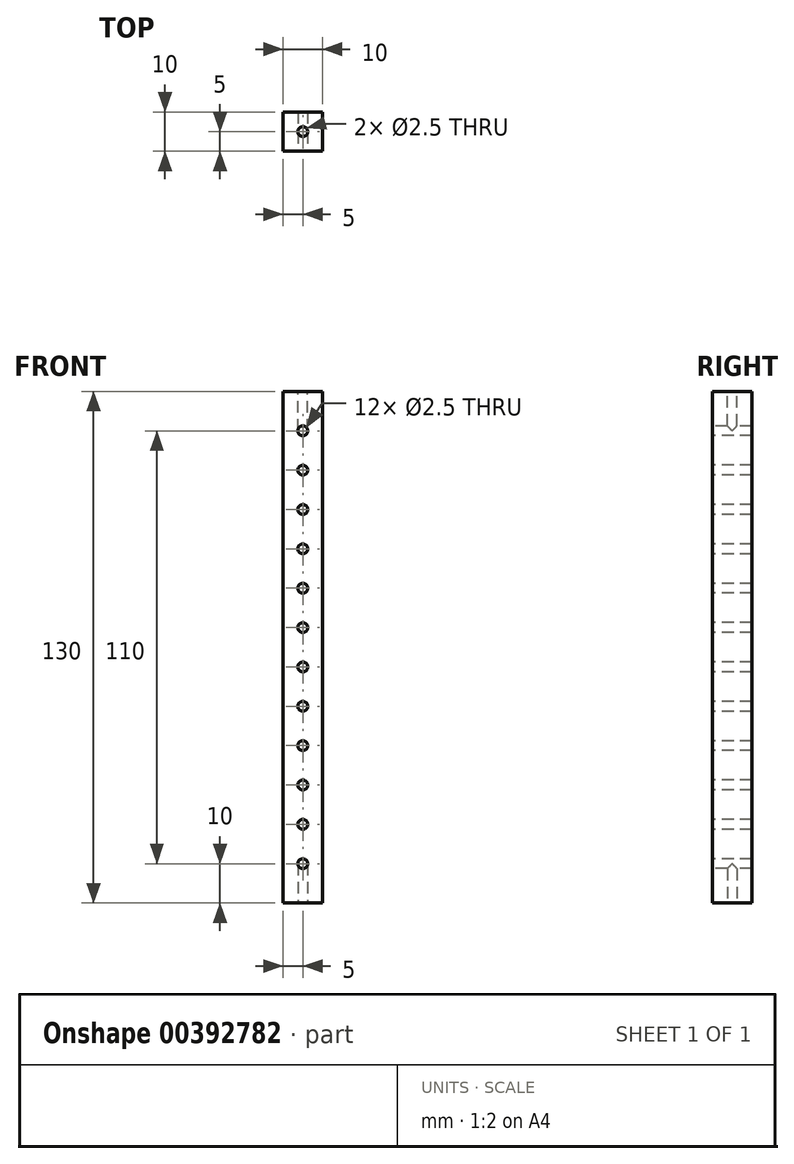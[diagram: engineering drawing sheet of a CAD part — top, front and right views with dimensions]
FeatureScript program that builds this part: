
annotation { "Feature Type Name" : "Feature", "Feature Type Description" : "" }
export const myFeature = defineFeature(function(context is Context, id is Id, definition is map)
    precondition{}
    {
        {
            var Q0;
            Q0=qCreatedBy(makeId("Top.planeOp"),FACE);
            var sketch = newSketch(context, id + "F0", { "sketchPlane" : qUnion([Q0])});
            skLineSegment(sketch, "E0.bottom", {"start": v(0, 0) * mm, "end": v(10, 0) * mm});
            skLineSegment(sketch, "E0.top", {"start": v(0, 10) * mm, "end": v(10, 10) * mm});
            skLineSegment(sketch, "E0.left", {"start": v(0, 0) * mm, "end": v(0, 10) * mm});
            skLineSegment(sketch, "E0.right", {"start": v(10, 0) * mm, "end": v(10, 10) * mm});
            skSolve(sketch);
        }
        {
            var Q0;
            Q0=makeQuery(id+"F0.imprint","IMPRINT",FACE,{"disambiguationData":[TD([[makeQuery(id+"F0.imprint","IMPRINT",EDGE,{"derivedFrom":sQuery(id+"F0.wireOp",EDGE,"E0.bottom")}),1.0]])]});
            extrude(context, id + "F1", {"entities" : qUnion([Q0]), "depth" : 130 * mm});
        }
        {
            var Q0;
            Q0=makeQuery(id+"F1.opExtrude","SWEPT_FACE",FACE,{"disambiguationData":[OSD([sQuery(id+"F0.wireOp",EDGE,"E0.bottom")])]});
            var sketch = newSketch(context, id + "F2", { "sketchPlane" : qUnion([Q0])});
            skLineSegment(sketch, "E1.bottom", {"start": v(0, 0) * mm, "end": v(5, 0) * mm});
            skLineSegment(sketch, "E1.top", {"start": v(0, 10) * mm, "end": v(5, 10) * mm});
            skLineSegment(sketch, "E1.left", {"start": v(0, 0) * mm, "end": v(0, 10) * mm});
            skLineSegment(sketch, "E1.right", {"start": v(5, 0) * mm, "end": v(5, 10) * mm});
            skLineSegment(sketch, "E2.bottom", {"start": v(5, 10) * mm, "end": v(10, 10) * mm});
            skLineSegment(sketch, "E2.top", {"start": v(5, 20) * mm, "end": v(10, 20) * mm});
            skLineSegment(sketch, "E2.left", {"start": v(5, 10) * mm, "end": v(5, 20) * mm});
            skLineSegment(sketch, "E2.right", {"start": v(10, 10) * mm, "end": v(10, 20) * mm});
            skLineSegment(sketch, "E3.bottom", {"start": v(5, 20) * mm, "end": v(0, 20) * mm});
            skLineSegment(sketch, "E3.top", {"start": v(5, 30) * mm, "end": v(0, 30) * mm});
            skLineSegment(sketch, "E3.left", {"start": v(5, 20) * mm, "end": v(5, 30) * mm});
            skLineSegment(sketch, "E3.right", {"start": v(0, 20) * mm, "end": v(0, 30) * mm});
            skSolve(sketch);
        }
        {
            var Q0;
            Q0=sQuery(id+"F2.wireOp",VERTEX,"E1.top.end");
            var Q1;
            Q1=sQuery(id+"F2.wireOp",VERTEX,"E3.bottom.start");
            var Q2;
            Q2=sQuery(id+"F2.wireOp",VERTEX,"E3.top.start");
            var Q3;
            Q3=makeQuery(id+"F1.opExtrude","SWEPT_BODY",BODY,{"disambiguationData":[OSD([sQuery(id+"F0.wireOp",EDGE,"E0.bottom"),sQuery(id+"F0.wireOp",EDGE,"E0.top"),sQuery(id+"F0.wireOp",EDGE,"E0.left"),sQuery(id+"F0.wireOp",EDGE,"E0.right")])]});
            hole(context, id + "F3", {"style" : HoleStyle.SIMPLE, "endStyle" : HoleEndStyle.BLIND, "holeDiameter" : 2.5 * mm, "holeDepth" : 10 * mm, "isTappedThrough" : true, "tappedDepth" : 12 * mm, "tapClearance" : 3, "locations" : qUnion([Q0, Q1, Q2]), "scope" : qUnion([Q3])});
        }
        {
            var Q0;
            Q0=makeQuery(id+"F1.opExtrude","SWEPT_FACE",FACE,{"disambiguationData":[OSD([sQuery(id+"F0.wireOp",EDGE,"E0.bottom")])]});
            var sketch = newSketch(context, id + "F4", { "sketchPlane" : qUnion([Q0])});
            skLineSegment(sketch, "E4.bottom", {"start": v(5, 30) * mm, "end": v(10, 30) * mm});
            skLineSegment(sketch, "E4.top", {"start": v(5, 40) * mm, "end": v(10, 40) * mm});
            skLineSegment(sketch, "E4.left", {"start": v(5, 30) * mm, "end": v(5, 40) * mm});
            skLineSegment(sketch, "E4.right", {"start": v(10, 30) * mm, "end": v(10, 40) * mm});
            skLineSegment(sketch, "E5.bottom", {"start": v(5, 40) * mm, "end": v(0, 40) * mm});
            skLineSegment(sketch, "E5.top", {"start": v(5, 50) * mm, "end": v(0, 50) * mm});
            skLineSegment(sketch, "E5.left", {"start": v(5, 40) * mm, "end": v(5, 50) * mm});
            skLineSegment(sketch, "E5.right", {"start": v(0, 40) * mm, "end": v(0, 50) * mm});
            skLineSegment(sketch, "E6.bottom", {"start": v(5, 50) * mm, "end": v(10, 50) * mm});
            skLineSegment(sketch, "E6.top", {"start": v(5, 60) * mm, "end": v(10, 60) * mm});
            skLineSegment(sketch, "E6.left", {"start": v(5, 50) * mm, "end": v(5, 60) * mm});
            skLineSegment(sketch, "E6.right", {"start": v(10, 50) * mm, "end": v(10, 60) * mm});
            skSolve(sketch);
        }
        {
            var Q0;
            Q0=sQuery(id+"F4.wireOp",VERTEX,"E4.top.start");
            var Q1;
            Q1=sQuery(id+"F4.wireOp",VERTEX,"E6.bottom.start");
            var Q2;
            Q2=sQuery(id+"F4.wireOp",VERTEX,"E6.top.start");
            var Q3;
            Q3=makeQuery(id+"F1.opExtrude","SWEPT_BODY",BODY,{"disambiguationData":[OSD([sQuery(id+"F0.wireOp",EDGE,"E0.bottom"),sQuery(id+"F0.wireOp",EDGE,"E0.top"),sQuery(id+"F0.wireOp",EDGE,"E0.left"),sQuery(id+"F0.wireOp",EDGE,"E0.right")])]});
            hole(context, id + "F5", {"style" : HoleStyle.SIMPLE, "endStyle" : HoleEndStyle.BLIND, "holeDiameter" : 2.5 * mm, "holeDepth" : 10 * mm, "isTappedThrough" : true, "tappedDepth" : 12 * mm, "tapClearance" : 3, "locations" : qUnion([Q0, Q1, Q2]), "scope" : qUnion([Q3])});
        }
        {
            var Q0;
            Q0=makeQuery(id+"F1.opExtrude","SWEPT_FACE",FACE,{"disambiguationData":[OSD([sQuery(id+"F0.wireOp",EDGE,"E0.bottom")])]});
            var sketch = newSketch(context, id + "F6", { "sketchPlane" : qUnion([Q0])});
            skLineSegment(sketch, "E7.bottom", {"start": v(5, 60) * mm, "end": v(10, 60) * mm});
            skLineSegment(sketch, "E7.top", {"start": v(5, 70) * mm, "end": v(10, 70) * mm});
            skLineSegment(sketch, "E7.left", {"start": v(5, 60) * mm, "end": v(5, 70) * mm});
            skLineSegment(sketch, "E7.right", {"start": v(10, 60) * mm, "end": v(10, 70) * mm});
            skLineSegment(sketch, "E8.bottom", {"start": v(5, 70) * mm, "end": v(0, 70) * mm});
            skLineSegment(sketch, "E8.top", {"start": v(5, 80) * mm, "end": v(0, 80) * mm});
            skLineSegment(sketch, "E8.left", {"start": v(5, 70) * mm, "end": v(5, 80) * mm});
            skLineSegment(sketch, "E8.right", {"start": v(0, 70) * mm, "end": v(0, 80) * mm});
            skLineSegment(sketch, "E9.bottom", {"start": v(5, 80) * mm, "end": v(10, 80) * mm});
            skLineSegment(sketch, "E9.top", {"start": v(5, 90) * mm, "end": v(10, 90) * mm});
            skLineSegment(sketch, "E9.left", {"start": v(5, 80) * mm, "end": v(5, 90) * mm});
            skLineSegment(sketch, "E9.right", {"start": v(10, 80) * mm, "end": v(10, 90) * mm});
            skLineSegment(sketch, "E10.bottom", {"start": v(5, 90) * mm, "end": v(0, 90) * mm});
            skLineSegment(sketch, "E10.top", {"start": v(5, 100) * mm, "end": v(0, 100) * mm});
            skLineSegment(sketch, "E10.left", {"start": v(5, 90) * mm, "end": v(5, 100) * mm});
            skLineSegment(sketch, "E10.right", {"start": v(0, 90) * mm, "end": v(0, 100) * mm});
            skLineSegment(sketch, "E11.bottom", {"start": v(5, 100) * mm, "end": v(10, 100) * mm});
            skLineSegment(sketch, "E11.top", {"start": v(5, 110) * mm, "end": v(10, 110) * mm});
            skLineSegment(sketch, "E11.left", {"start": v(5, 100) * mm, "end": v(5, 110) * mm});
            skLineSegment(sketch, "E11.right", {"start": v(10, 100) * mm, "end": v(10, 110) * mm});
            skSolve(sketch);
        }
        {
            var Q0;
            Q0=sQuery(id+"F6.wireOp",VERTEX,"E8.top.start");
            var Q1;
            Q1=sQuery(id+"F6.wireOp",VERTEX,"E10.bottom.start");
            var Q2;
            Q2=sQuery(id+"F6.wireOp",VERTEX,"E10.top.start");
            var Q3;
            Q3=sQuery(id+"F6.wireOp",VERTEX,"E11.left.end");
            var Q4;
            Q4=makeQuery(id+"F1.opExtrude","SWEPT_BODY",BODY,{"disambiguationData":[OSD([sQuery(id+"F0.wireOp",EDGE,"E0.bottom"),sQuery(id+"F0.wireOp",EDGE,"E0.top"),sQuery(id+"F0.wireOp",EDGE,"E0.left"),sQuery(id+"F0.wireOp",EDGE,"E0.right")])]});
            hole(context, id + "F7", {"style" : HoleStyle.SIMPLE, "endStyle" : HoleEndStyle.BLIND, "holeDiameter" : 2.5 * mm, "holeDepth" : 10 * mm, "isTappedThrough" : true, "tappedDepth" : 12 * mm, "tapClearance" : 3, "locations" : qUnion([Q0, Q1, Q2, Q3]), "scope" : qUnion([Q4])});
        }
        {
            var Q0;
            Q0=makeQuery(id+"F1.opExtrude","SWEPT_FACE",FACE,{"disambiguationData":[OSD([sQuery(id+"F0.wireOp",EDGE,"E0.bottom")])]});
            var sketch = newSketch(context, id + "F8", { "sketchPlane" : qUnion([Q0])});
            skLineSegment(sketch, "E12.bottom", {"start": v(5, 80) * mm, "end": v(10, 80) * mm});
            skLineSegment(sketch, "E12.top", {"start": v(5, 70) * mm, "end": v(10, 70) * mm});
            skLineSegment(sketch, "E12.left", {"start": v(5, 80) * mm, "end": v(5, 70) * mm});
            skLineSegment(sketch, "E12.right", {"start": v(10, 80) * mm, "end": v(10, 70) * mm});
            skSolve(sketch);
        }
        {
            var Q0;
            Q0=sQuery(id+"F8.wireOp",VERTEX,"E12.left.end");
            var Q1;
            Q1=makeQuery(id+"F1.opExtrude","SWEPT_BODY",BODY,{"disambiguationData":[OSD([sQuery(id+"F0.wireOp",EDGE,"E0.bottom"),sQuery(id+"F0.wireOp",EDGE,"E0.top"),sQuery(id+"F0.wireOp",EDGE,"E0.left"),sQuery(id+"F0.wireOp",EDGE,"E0.right")])]});
            hole(context, id + "F9", {"style" : HoleStyle.SIMPLE, "endStyle" : HoleEndStyle.BLIND, "holeDiameter" : 2.5 * mm, "holeDepth" : 10 * mm, "isTappedThrough" : true, "tappedDepth" : 12 * mm, "tapClearance" : 3, "locations" : qUnion([Q0]), "scope" : qUnion([Q1])});
        }
        {
            var Q0;
            Q0=makeQuery(id+"F1.opExtrude","SWEPT_FACE",FACE,{"disambiguationData":[OSD([sQuery(id+"F0.wireOp",EDGE,"E0.bottom")])]});
            var sketch = newSketch(context, id + "F10", { "sketchPlane" : qUnion([Q0])});
            skLineSegment(sketch, "E13.bottom", {"start": v(5, 110) * mm, "end": v(0, 110) * mm});
            skLineSegment(sketch, "E13.top", {"start": v(5, 120) * mm, "end": v(0, 120) * mm});
            skLineSegment(sketch, "E13.left", {"start": v(5, 110) * mm, "end": v(5, 120) * mm});
            skLineSegment(sketch, "E13.right", {"start": v(0, 110) * mm, "end": v(0, 120) * mm});
            skSolve(sketch);
        }
        {
            var Q0;
            Q0=sQuery(id+"F10.wireOp",VERTEX,"E13.top.start");
            var Q1;
            Q1=makeQuery(id+"F1.opExtrude","SWEPT_BODY",BODY,{"disambiguationData":[OSD([sQuery(id+"F0.wireOp",EDGE,"E0.bottom"),sQuery(id+"F0.wireOp",EDGE,"E0.top"),sQuery(id+"F0.wireOp",EDGE,"E0.left"),sQuery(id+"F0.wireOp",EDGE,"E0.right")])]});
            hole(context, id + "F11", {"style" : HoleStyle.SIMPLE, "endStyle" : HoleEndStyle.BLIND, "holeDiameter" : 2.5 * mm, "holeDepth" : 10 * mm, "isTappedThrough" : true, "tappedDepth" : 12 * mm, "tapClearance" : 3, "locations" : qUnion([Q0]), "scope" : qUnion([Q1])});
        }
        {
            var Q0;
            Q0=makeQuery(id+"F1.opExtrude","CAP_FACE",FACE,{"disambiguationData":[OSD([sQuery(id+"F0.wireOp",EDGE,"E0.bottom"),sQuery(id+"F0.wireOp",EDGE,"E0.top"),sQuery(id+"F0.wireOp",EDGE,"E0.left"),sQuery(id+"F0.wireOp",EDGE,"E0.right")])],"isStart":false});
            var sketch = newSketch(context, id + "F12", { "sketchPlane" : qUnion([Q0])});
            skLineSegment(sketch, "E14.bottom", {"start": v(0, 0) * mm, "end": v(5, 0) * mm});
            skLineSegment(sketch, "E14.top", {"start": v(0, 5) * mm, "end": v(5, 5) * mm});
            skLineSegment(sketch, "E14.left", {"start": v(0, 0) * mm, "end": v(0, 5) * mm});
            skLineSegment(sketch, "E14.right", {"start": v(5, 0) * mm, "end": v(5, 5) * mm});
            skSolve(sketch);
        }
        {
            var Q0;
            Q0=sQuery(id+"F12.wireOp",VERTEX,"E14.top.end");
            var Q1;
            Q1=makeQuery(id+"F1.opExtrude","SWEPT_BODY",BODY,{"disambiguationData":[OSD([sQuery(id+"F0.wireOp",EDGE,"E0.bottom"),sQuery(id+"F0.wireOp",EDGE,"E0.top"),sQuery(id+"F0.wireOp",EDGE,"E0.left"),sQuery(id+"F0.wireOp",EDGE,"E0.right")])]});
            hole(context, id + "F13", {"style" : HoleStyle.SIMPLE, "endStyle" : HoleEndStyle.BLIND, "holeDiameter" : 2.5 * mm, "holeDepth" : 10 * mm, "isTappedThrough" : true, "tappedDepth" : 12 * mm, "tapClearance" : 3, "locations" : qUnion([Q0]), "scope" : qUnion([Q1])});
        }
        {
            var Q0;
            Q0=makeQuery(id+"F1.opExtrude","CAP_FACE",FACE,{"disambiguationData":[OSD([sQuery(id+"F0.wireOp",EDGE,"E0.bottom"),sQuery(id+"F0.wireOp",EDGE,"E0.top"),sQuery(id+"F0.wireOp",EDGE,"E0.left"),sQuery(id+"F0.wireOp",EDGE,"E0.right")])],"isStart":true});
            var sketch = newSketch(context, id + "F14", { "sketchPlane" : qUnion([Q0])});
            skLineSegment(sketch, "E15.bottom", {"start": v(10, 0) * mm, "end": v(5, 0) * mm});
            skLineSegment(sketch, "E15.top", {"start": v(10, -5) * mm, "end": v(5, -5) * mm});
            skLineSegment(sketch, "E15.left", {"start": v(10, 0) * mm, "end": v(10, -5) * mm});
            skLineSegment(sketch, "E15.right", {"start": v(5, 0) * mm, "end": v(5, -5) * mm});
            skSolve(sketch);
        }
        {
            var Q0;
            Q0=sQuery(id+"F14.wireOp",VERTEX,"E15.top.end");
            var Q1;
            Q1=makeQuery(id+"F1.opExtrude","SWEPT_BODY",BODY,{"disambiguationData":[OSD([sQuery(id+"F0.wireOp",EDGE,"E0.bottom"),sQuery(id+"F0.wireOp",EDGE,"E0.top"),sQuery(id+"F0.wireOp",EDGE,"E0.left"),sQuery(id+"F0.wireOp",EDGE,"E0.right")])]});
            hole(context, id + "F15", {"style" : HoleStyle.SIMPLE, "endStyle" : HoleEndStyle.BLIND, "holeDiameter" : 2.5 * mm, "holeDepth" : 10 * mm, "isTappedThrough" : true, "tappedDepth" : 12 * mm, "tapClearance" : 3, "locations" : qUnion([Q0]), "scope" : qUnion([Q1])});
        }
    });
